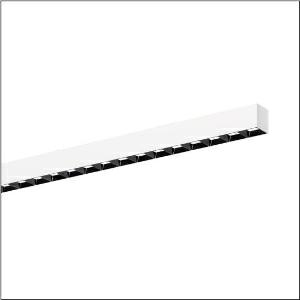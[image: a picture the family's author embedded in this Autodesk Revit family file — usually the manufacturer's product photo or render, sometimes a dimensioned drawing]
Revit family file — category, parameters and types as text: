
# Revit family: silica_r__21_51mx24dc3awb_4576
name_source: partatom
category: Lighting Fixtures
units: mm (PartAtom-declared; Revit-internal decimal feet)

## family parameters
Cut with Voids When Loaded = No
Host = Face
Light Source = No
Part Type = Normal
Room Calculation Point = No
Round Connector Dimension = Use Diameter
Shared = No

## types (1)
- --- (1 x LED, 10800 lm, 79 W, 3000K)
    Apparent Load = 79 VA
    CIE Flux Codes = 74 94 99 100 100
    Color Rendering = 80
    Color Temperature = 3000K
    Default Elevation = 1800 mm
    Description = Silica® 21, office luminaire, primary light control with darklight reflector, of PMMA, black, CAT 2 (L<= 3000cd/m²), light emission: direct distribution, primary light characteristic: asymmetric, installation type: surface-mounted, LED, rated luminous flux: 10.800lm, luminous efficacy: 137lm/W, light colour: 830, colour temperature: 3000K, with terminal, 3+2-pole, max. 2.5mm², mains connection: 220..240V, AC, 50/60Hz, rated input power: 79W, luminaire housing, of aluminium, traffic white (RAL 9016), length: 3.004mm, width: 53mm, height: 53mm, protection rating (complete): IP20, insulation class (complete): insulation class I (protective earthing), certification: CE, permissible operating ambient temperature: 0..+35°C, standard: EN 50419, packaging unit: 1 piece
    Height = 0 mm  [stored 0 ft]
    Lamp = 1 x LED
    Lamp Light Flux = 10800 lm
    Lamp Power = 79 W
    Lamp count = 1
    Length = 3004 mm
    Luminous efficacy = 137 lm/W
    Manufacturer = Siteco
    ModVariant = No
    Model = 51MX24DC3AWB
    Mounting Place = Ceiling
    Mounting Type = Recessed
    Number of Poles = 1
    OnlyDefault = Yes
    Power Factor = 1
    Product Name = Silica® 21
    Product group = office luminaire | ceiling recessed
    ProductGroupID = 401
    Protection Class = Protection class I
    Protection Degree = IP 20
    RLX_Detail_Level = 1
    RLX_Emergency_Light_Flux = 0 lm
    RLX_Emergency_Type = 0
    RLX_Emergency_Type_DB = No
    RlxData = <blob elided: 62465 chars, md5=cf322cb0>
    Socket = socket
    Standby Power = 0 W
    System Light Flux = 10800 lm
    System Power = 79 W
    Type Comments = factory setting: luminous flux: 100 % | dim-lin: 254 | 448 mA
    Type Image = l_1313592.jpg
    URL = http://relux.com
    VarID = @adj_071929
    Voltage = 0 V
    Weight = 0.00 kg
    Width = 53 mm

note: [stored X ft] marks values corroborated as IEEE doubles in the binary element streams (Revit-internal decimal feet)

## geometry (parser evidence)
native form markers: Blend x4, Sweep x10
no freeform markers — native parametric forms only
